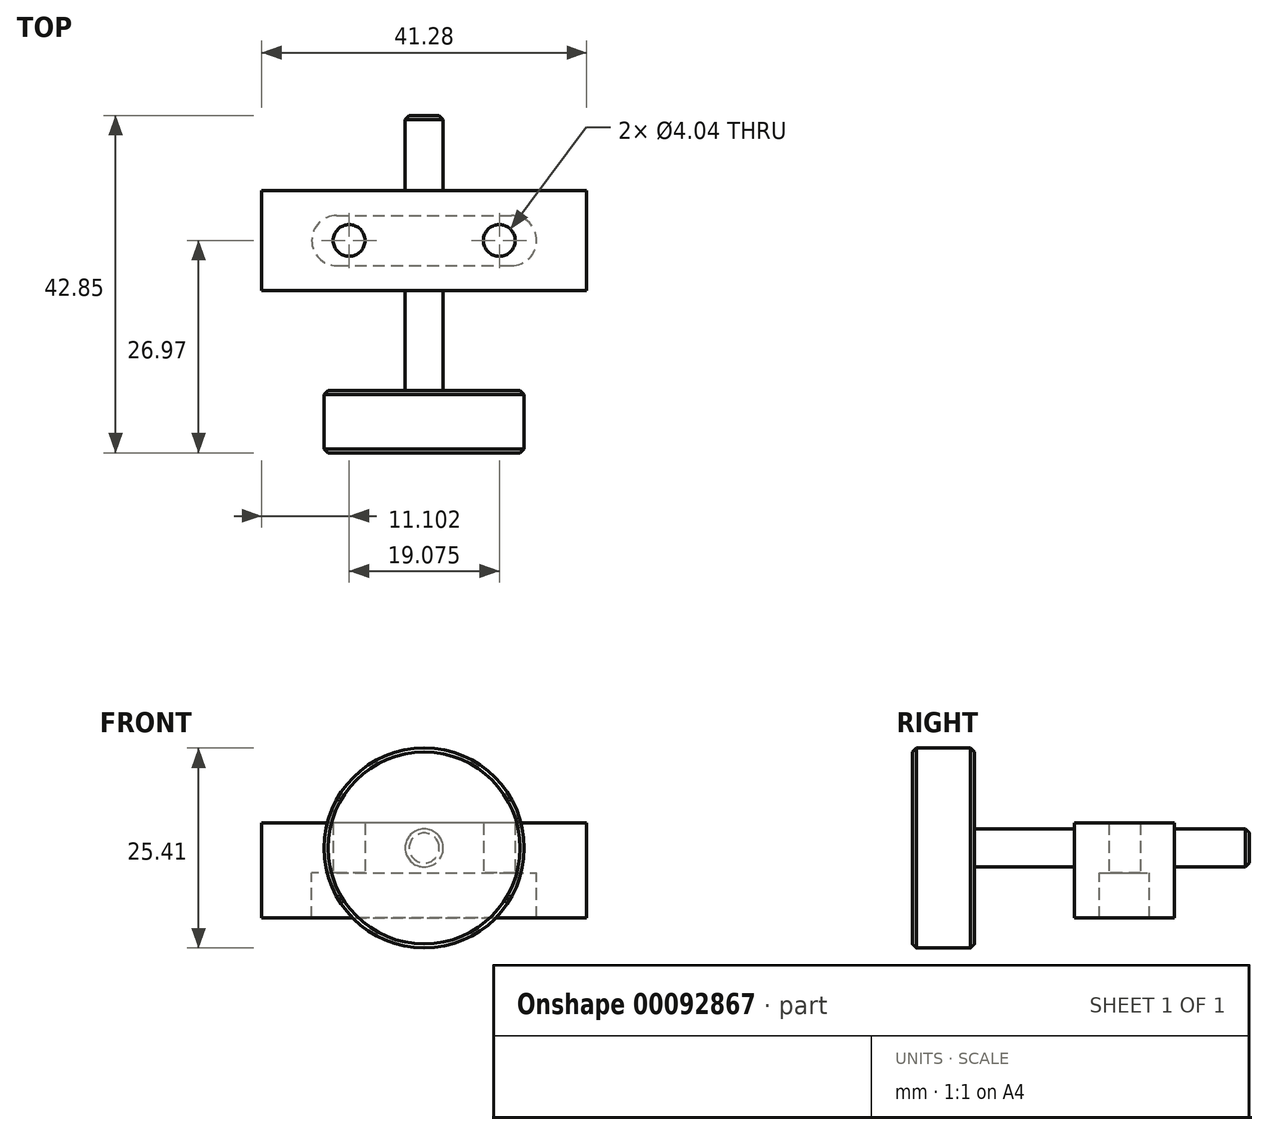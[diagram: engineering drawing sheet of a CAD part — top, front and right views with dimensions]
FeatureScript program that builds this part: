
annotation { "Feature Type Name" : "Feature", "Feature Type Description" : "" }
export const myFeature = defineFeature(function(context is Context, id is Id, definition is map)
    precondition{}
    {
        {
            var Q0;
            Q0=qCreatedBy(makeId("Top.planeOp"),FACE);
            var sketch = newSketch(context, id + "F0", { "sketchPlane" : qUnion([Q0])});
            skLineSegment(sketch, "E0.bottom", {"start": v(20.64, -6.35) * mm, "end": v(-20.64, -6.35) * mm});
            skLineSegment(sketch, "E0.top", {"start": v(20.64, 6.35) * mm, "end": v(-20.64, 6.35) * mm});
            skLineSegment(sketch, "E0.left", {"start": v(20.64, -6.35) * mm, "end": v(20.64, 6.35) * mm});
            skLineSegment(sketch, "E0.right", {"start": v(-20.64, -6.35) * mm, "end": v(-20.64, 6.35) * mm});
            skPoint(sketch, "E0.middle", {"position": v(0, 0) * mm});
            skSolve(sketch);
        }
        {
            var Q0;
            Q0=makeQuery(id+"F0.imprint","IMPRINT",FACE,{"disambiguationData":[TD([[makeQuery(id+"F0.imprint","IMPRINT",EDGE,{"derivedFrom":sQuery(id+"F0.wireOp",EDGE,"E0.bottom")}),-1.0]])]});
            extrude(context, id + "F1", {"entities" : qUnion([Q0]), "depth" : 6.35 * mm});
        }
        {
            var Q0;
            Q0=makeQuery(id+"F1.opExtrude","CAP_FACE",FACE,{"disambiguationData":[OSD([sQuery(id+"F0.wireOp",EDGE,"E0.bottom"),sQuery(id+"F0.wireOp",EDGE,"E0.top"),sQuery(id+"F0.wireOp",EDGE,"E0.left"),sQuery(id+"F0.wireOp",EDGE,"E0.right")])],"isStart":true});
            var sketch = newSketch(context, id + "F2", { "sketchPlane" : qUnion([Q0])});
            skLineSegment(sketch, "E1", {"start": v(-11.11, 6.35) * mm, "end": v(-11.11, -6.35) * mm, "construction": true});
            skLineSegment(sketch, "E2", {"start": v(11.11, 6.35) * mm, "end": v(11.11, -6.35) * mm, "construction": true});
            skLineSegment(sketch, "E3", {"start": v(-11.11, 0) * mm, "end": v(11.11, 0) * mm, "construction": true});
            skArc(sketch, "E4.0.startCap", {"start": v(-11.11, -3.17) * mm, "mid": v(-14.29, 0) * mm, "end": v(-11.11, 3.18) * mm});
            skArc(sketch, "E4.0.endCap", {"start": v(11.11, 3.17) * mm, "mid": v(14.29, 0) * mm, "end": v(11.11, -3.18) * mm});
            skLineSegment(sketch, "E4.0.left", {"start": v(-11.11, 3.18) * mm, "end": v(11.11, 3.17) * mm});
            skLineSegment(sketch, "E4.0.right", {"start": v(-11.11, -3.17) * mm, "end": v(11.11, -3.18) * mm});
            skSolve(sketch);
        }
        {
            var Q0;
            Q0=makeQuery(id+"F2.imprint","IMPRINT",FACE,{"disambiguationData":[TD([[makeQuery(id+"F2.imprint","IMPRINT",EDGE,{"derivedFrom":sQuery(id+"F2.wireOp",EDGE,"E4.0.startCap")}),-1.0]])]});
            extrude(context, id + "F3", {"entities" : qUnion([Q0]), "operationType" : NewBodyOperationType.ADD, "depth" : 5.7 * mm});
        }
        {
            var Q0;
            Q0=makeQuery(id+"F3.opExtrude","CAP_FACE",FACE,{"disambiguationData":[OSD([sQuery(id+"F2.wireOp",EDGE,"E4.0.startCap"),sQuery(id+"F2.wireOp",EDGE,"E4.0.endCap"),sQuery(id+"F2.wireOp",EDGE,"E4.0.left"),sQuery(id+"F2.wireOp",EDGE,"E4.0.right")])],"isStart":false});
            var sketch = newSketch(context, id + "F4", { "sketchPlane" : qUnion([Q0])});
            skArc(sketch, "E5.0.0", {"start": v(-11.11, 3.18) * mm, "mid": v(-14.29, 0) * mm, "end": v(-11.11, -3.17) * mm, "construction": true});
            skLineSegment(sketch, "E5.0.1", {"start": v(-11.11, -3.17) * mm, "end": v(11.11, -3.18) * mm, "construction": true});
            skArc(sketch, "E5.0.2", {"start": v(11.11, -3.18) * mm, "mid": v(14.29, 0) * mm, "end": v(11.11, 3.17) * mm, "construction": true});
            skLineSegment(sketch, "E5.0.3", {"start": v(11.11, 3.17) * mm, "end": v(-11.11, 3.18) * mm, "construction": true});
            skLineSegment(sketch, "E6", {"start": v(-9.54, 3.18) * mm, "end": v(-9.54, -3.17) * mm, "construction": true});
            skLineSegment(sketch, "E7", {"start": v(9.54, 3.17) * mm, "end": v(9.54, -3.18) * mm, "construction": true});
            skPoint(sketch, "E8", {"position": v(-9.54, 0) * mm});
            skPoint(sketch, "E9", {"position": v(9.54, 0) * mm});
            skSolve(sketch);
        }
        {
            var Q0;
            Q0=sQuery(id+"F4.wireOp",VERTEX,"E8");
            var Q1;
            Q1=sQuery(id+"F4.wireOp",VERTEX,"E9");
            var Q2;
            Q2=makeQuery(id+"F1.opExtrude","SWEPT_BODY",BODY,{"disambiguationData":[OSD([sQuery(id+"F0.wireOp",EDGE,"E0.bottom"),sQuery(id+"F0.wireOp",EDGE,"E0.top"),sQuery(id+"F0.wireOp",EDGE,"E0.left"),sQuery(id+"F0.wireOp",EDGE,"E0.right")])]});
            hole(context, id + "F5", {"style" : HoleStyle.SIMPLE, "endStyle" : HoleEndStyle.BLIND, "standardTappedOrClearance" : lookupTablePath({ "standard" : "ANSI", "engagement" : "75%", "pitch" : "32 tpi", "size" : "#10", "type" : "Tapped" }), "standardBlindInLast" : lookupTablePath({ "standard" : "ANSI", "engagement" : "75%", "pitch" : "32 tpi", "size" : "#10", "type" : "Tapped" }), "holeDiameter" : 4.04 * mm, "holeDepth" : 10.16 * mm, "locations" : qUnion([Q0, Q1]), "scope" : qUnion([Q2]), "majorDiameter" : 4.83 * mm});
        }
        {
            var Q0;
            Q0=makeQuery(id+"F1.opExtrude","SWEPT_FACE",FACE,{"disambiguationData":[OSD([sQuery(id+"F0.wireOp",EDGE,"E0.bottom")])]});
            var sketch = newSketch(context, id + "F6", { "sketchPlane" : qUnion([Q0])});
            skLineSegment(sketch, "E10", {"start": v(-20.64, 3.18) * mm, "end": v(20.64, 3.18) * mm, "construction": true});
            skPoint(sketch, "E11", {"position": v(0, 3.18) * mm});
            skSolve(sketch);
        }
        {
            var Q0;
            Q0=sQuery(id+"F6.wireOp",VERTEX,"E11");
            var Q1;
            Q1=makeQuery(id+"F1.opExtrude","SWEPT_BODY",BODY,{"disambiguationData":[OSD([sQuery(id+"F0.wireOp",EDGE,"E0.bottom"),sQuery(id+"F0.wireOp",EDGE,"E0.top"),sQuery(id+"F0.wireOp",EDGE,"E0.left"),sQuery(id+"F0.wireOp",EDGE,"E0.right")])]});
            hole(context, id + "F7", {"style" : HoleStyle.SIMPLE, "endStyle" : HoleEndStyle.THROUGH, "standardTappedOrClearance" : lookupTablePath({ "standard" : "ANSI", "engagement" : "75%", "pitch" : "32 tpi", "size" : "#10", "type" : "Tapped" }), "standardBlindInLast" : lookupTablePath({ "standard" : "ANSI", "engagement" : "75%", "pitch" : "32 tpi", "size" : "#10", "type" : "Tapped" }), "holeDiameter" : 4.04 * mm, "locations" : qUnion([Q0]), "scope" : qUnion([Q1]), "isTappedThrough" : true, "majorDiameter" : 4.83 * mm, "showTappedDepth" : true});
        }
        {
            var Q0;
            Q0=makeQuery(id+"F1.opExtrude","SWEPT_FACE",FACE,{"disambiguationData":[OSD([sQuery(id+"F0.wireOp",EDGE,"E0.bottom")])]});
            cPlane(context, id + "F8", {"entities" : qUnion([Q0]), "cplaneType" : CPlaneType.OFFSET, "offset" : 12.7 * mm, "width" : 152.4 * mm, "height" : 152.4 * mm});
        }
        {
            var Q0;
            Q0=qCreatedBy(id+"F8.planeOp",FACE);
            var sketch = newSketch(context, id + "F9", { "sketchPlane" : qUnion([Q0])});
            skCircle(sketch, "E12.0", {"center": v(0, 3.18) * mm, "radius": 2.02 * mm, "construction": true});
            skCircle(sketch, "E13", {"center": v(0, 3.18) * mm, "radius": 12.7 * mm});
            skSolve(sketch);
        }
        {
            var Q0;
            Q0=makeQuery(id+"F9.imprint","IMPRINT",FACE,{"disambiguationData":[TD([[makeQuery(id+"F9.imprint","IMPRINT",EDGE,{"derivedFrom":sQuery(id+"F9.wireOp",EDGE,"E13")}),1.0]])]});
            extrude(context, id + "F10", {"entities" : qUnion([Q0]), "depth" : 7.92 * mm});
        }
        {
            var Q0;
            Q0=makeQuery(id+"F10.opExtrude","CAP_FACE",FACE,{"disambiguationData":[OSD([sQuery(id+"F9.wireOp",EDGE,"E13")])],"isStart":true});
            var sketch = newSketch(context, id + "F11", { "sketchPlane" : qUnion([Q0])});
            skCircle(sketch, "E14.0.0", {"center": v(0, 3.18) * mm, "radius": 12.7 * mm, "construction": true});
            skCircle(sketch, "E15", {"center": v(0, 3.18) * mm, "radius": 2.41 * mm});
            skSolve(sketch);
        }
        {
            var Q0;
            Q0=makeQuery(id+"F11.imprint","IMPRINT",FACE,{"disambiguationData":[TD([[makeQuery(id+"F11.imprint","IMPRINT",EDGE,{"derivedFrom":sQuery(id+"F11.wireOp",EDGE,"E15")}),1.0]])]});
            extrude(context, id + "F12", {"entities" : qUnion([Q0]), "operationType" : NewBodyOperationType.ADD, "depth" : 34.92 * mm});
        }
        {
            var Q0;
            Q0=makeQuery(id+"F10.opExtrude","CAP_EDGE",EDGE,{"disambiguationData":[OSD([sQuery(id+"F9.wireOp",EDGE,"E13")])],"isStart":false});
            var Q1;
            Q1=makeQuery(id+"F10.opExtrude","CAP_EDGE",EDGE,{"disambiguationData":[OSD([sQuery(id+"F9.wireOp",EDGE,"E13")])],"isStart":true});
            var Q2;
            Q2=makeQuery(id+"F12.opExtrude","CAP_EDGE",EDGE,{"disambiguationData":[OSD([sQuery(id+"F11.wireOp",EDGE,"E15")])],"isStart":false});
            chamfer(context, id + "F13", {"entities" : qUnion([Q0, Q1, Q2]), "width" : 0.5 * mm, "tangentPropagation" : true});
        }
    });
